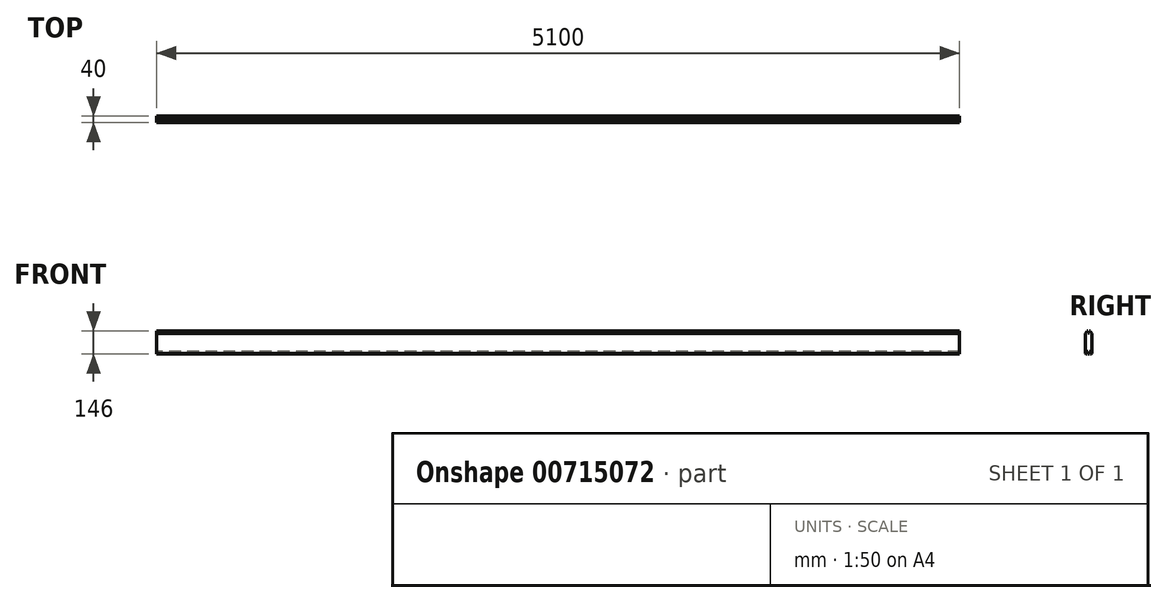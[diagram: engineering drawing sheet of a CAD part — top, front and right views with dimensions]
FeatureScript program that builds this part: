
annotation { "Feature Type Name" : "Feature", "Feature Type Description" : "" }
export const myFeature = defineFeature(function(context is Context, id is Id, definition is map)
    precondition{}
    {
        {
            var Q0;
            Q0=qCreatedBy(makeId("Right.planeOp"),FACE);
            var sketch = newSketch(context, id + "F0", { "sketchPlane" : qUnion([Q0])});
            skLineSegment(sketch, "E0", {"start": v(20, 56) * mm, "end": v(20, -70) * mm});
            skLineSegment(sketch, "E1", {"start": v(20, -70) * mm, "end": v(17, -73) * mm});
            skLineSegment(sketch, "E2", {"start": v(17, -73) * mm, "end": v(12, -73) * mm});
            skLineSegment(sketch, "E3", {"start": v(12, -59) * mm, "end": v(12, -73) * mm});
            skLineSegment(sketch, "E4", {"start": v(12, -59) * mm, "end": v(4, -59) * mm});
            skLineSegment(sketch, "E5", {"start": v(4, -73) * mm, "end": v(4, -59) * mm});
            skLineSegment(sketch, "E6", {"start": v(4, -73) * mm, "end": v(-4, -73) * mm});
            skLineSegment(sketch, "E7", {"start": v(-4, -59) * mm, "end": v(-4, -73) * mm});
            skLineSegment(sketch, "E8", {"start": v(-4, -59) * mm, "end": v(-12, -59) * mm});
            skLineSegment(sketch, "E9", {"start": v(-12, -73) * mm, "end": v(-12, -59) * mm});
            skLineSegment(sketch, "E10", {"start": v(-12, -73) * mm, "end": v(-17, -73) * mm});
            skLineSegment(sketch, "E11", {"start": v(-17, -73) * mm, "end": v(-20, -70) * mm});
            skLineSegment(sketch, "E12", {"start": v(-20, -70) * mm, "end": v(-20, 56) * mm});
            skLineSegment(sketch, "E13", {"start": v(-20, 56) * mm, "end": v(-17, 59) * mm});
            skLineSegment(sketch, "E14", {"start": v(-17, 59) * mm, "end": v(-12, 59) * mm});
            skLineSegment(sketch, "E15", {"start": v(-4, 59) * mm, "end": v(4, 59) * mm});
            skLineSegment(sketch, "E16", {"start": v(12, 59) * mm, "end": v(17, 59) * mm});
            skLineSegment(sketch, "E17", {"start": v(17, 59) * mm, "end": v(20, 56) * mm});
            skPoint(sketch, "E18.end.orphan", {"position": v(12, 57.8) * mm});
            skPoint(sketch, "E19.end.orphan", {"position": v(4, 66.3) * mm});
            skPoint(sketch, "E20.end.orphan", {"position": v(-4, 66.3) * mm});
            skLineSegment(sketch, "E21", {"start": v(-12, 59) * mm, "end": v(-12, 73) * mm});
            skLineSegment(sketch, "E22", {"start": v(-12, 73) * mm, "end": v(-4, 73) * mm});
            skLineSegment(sketch, "E23", {"start": v(-4, 73) * mm, "end": v(-4, 59) * mm});
            skLineSegment(sketch, "E24", {"start": v(4, 59) * mm, "end": v(4, 73) * mm});
            skLineSegment(sketch, "E25", {"start": v(4, 73) * mm, "end": v(12, 73) * mm});
            skLineSegment(sketch, "E26", {"start": v(12, 73) * mm, "end": v(12, 59) * mm});
            skSolve(sketch);
        }
        {
            var Q0;
            Q0=makeQuery(id+"F0.imprint","IMPRINT",FACE,{"disambiguationData":[TD([[makeQuery(id+"F0.imprint","IMPRINT",EDGE,{"derivedFrom":sQuery(id+"F0.wireOp",EDGE,"E0")}),-1.0]])]});
            extrude(context, id + "F1", {"entities" : qUnion([Q0]), "endBound" : BoundingType.SYMMETRIC, "depth" : 5100 * mm, "offsetDistance" : 25 * mm});
        }
    });
